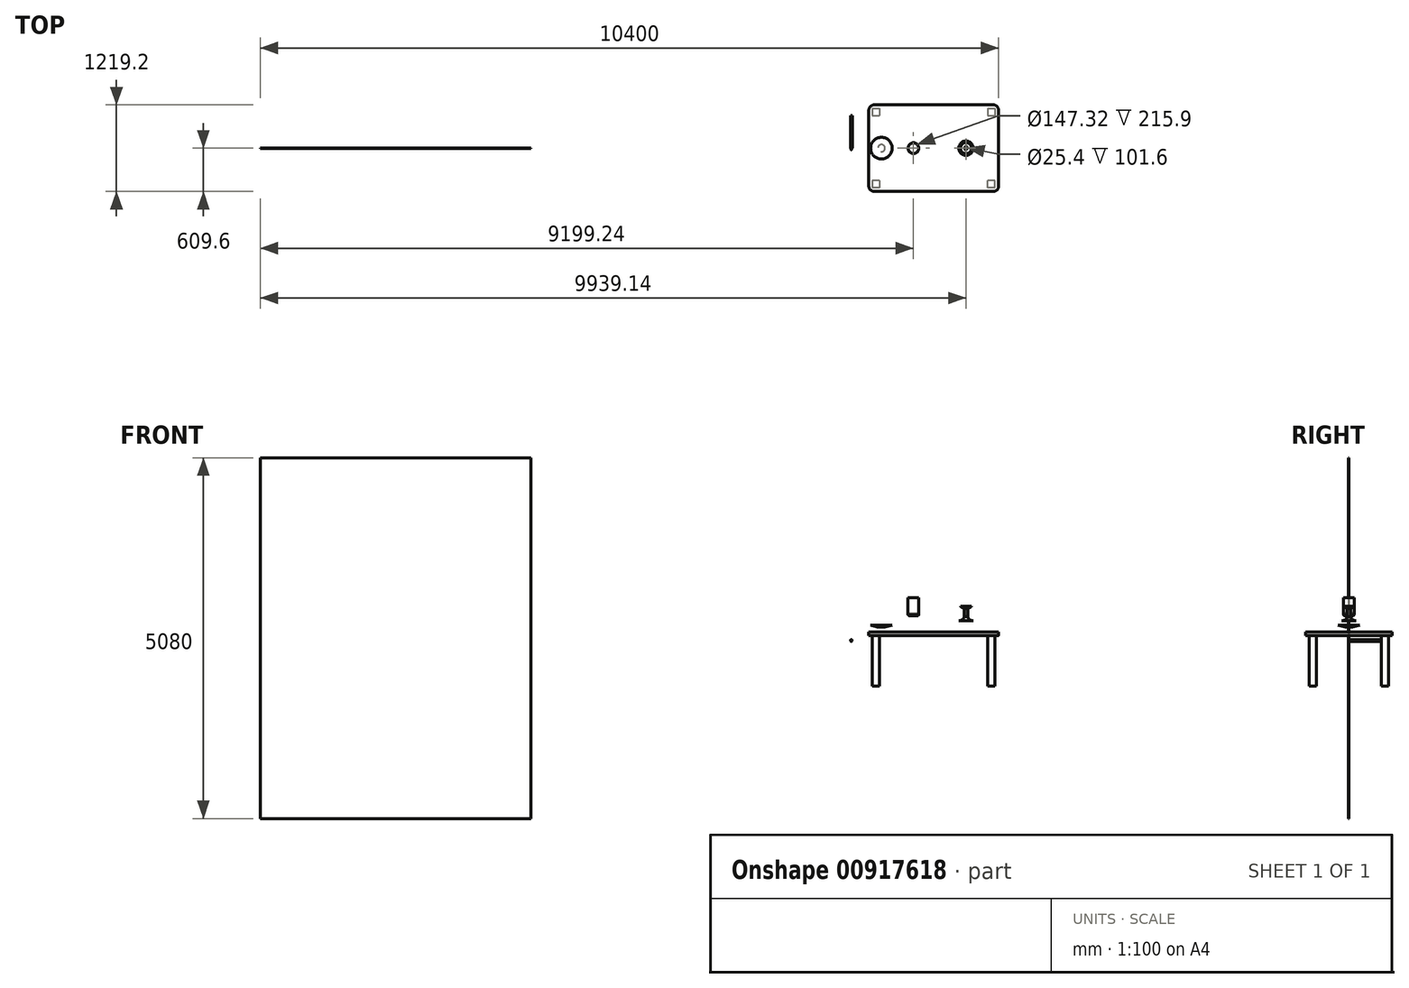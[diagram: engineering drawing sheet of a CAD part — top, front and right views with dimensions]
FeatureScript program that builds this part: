
annotation { "Feature Type Name" : "Feature", "Feature Type Description" : "" }
export const myFeature = defineFeature(function(context is Context, id is Id, definition is map)
    precondition{}
    {
        {
            var Q0;
            Q0=qCreatedBy(makeId("Top.planeOp"),FACE);
            var sketch = newSketch(context, id + "F0", { "sketchPlane" : qUnion([Q0])});
            skLineSegment(sketch, "E0.bottom", {"start": v(-838.2, 609.6) * mm, "end": v(838.2, 609.6) * mm});
            skLineSegment(sketch, "E0.top", {"start": v(-838.2, -609.6) * mm, "end": v(838.2, -609.6) * mm});
            skLineSegment(sketch, "E0.left", {"start": v(-914.4, 533.4) * mm, "end": v(-914.4, -533.4) * mm});
            skLineSegment(sketch, "E0.right", {"start": v(914.4, 533.4) * mm, "end": v(914.4, -533.4) * mm});
            skPoint(sketch, "E0.middle", {"position": v(0, 0) * mm});
            skLineSegment(sketch, "E1.bottom", {"start": v(-863.6, 558.8) * mm, "end": v(-762, 558.8) * mm});
            skLineSegment(sketch, "E1.top", {"start": v(-863.6, 457.2) * mm, "end": v(-762, 457.2) * mm});
            skLineSegment(sketch, "E1.left", {"start": v(-863.6, 558.8) * mm, "end": v(-863.6, 457.2) * mm});
            skLineSegment(sketch, "E1.right", {"start": v(-762, 558.8) * mm, "end": v(-762, 457.2) * mm});
            skLineSegment(sketch, "E2.bottom", {"start": v(762, 558.8) * mm, "end": v(863.6, 558.8) * mm});
            skLineSegment(sketch, "E2.top", {"start": v(762, 457.2) * mm, "end": v(863.6, 457.2) * mm});
            skLineSegment(sketch, "E2.left", {"start": v(762, 558.8) * mm, "end": v(762, 457.2) * mm});
            skLineSegment(sketch, "E2.right", {"start": v(863.6, 558.8) * mm, "end": v(863.6, 457.2) * mm});
            skLineSegment(sketch, "E3.bottom", {"start": v(863.6, -558.8) * mm, "end": v(762, -558.8) * mm});
            skLineSegment(sketch, "E3.top", {"start": v(863.6, -457.2) * mm, "end": v(762, -457.2) * mm});
            skLineSegment(sketch, "E3.left", {"start": v(863.6, -558.8) * mm, "end": v(863.6, -457.2) * mm});
            skLineSegment(sketch, "E3.right", {"start": v(762, -558.8) * mm, "end": v(762, -457.2) * mm});
            skLineSegment(sketch, "E4.bottom", {"start": v(-762, -457.2) * mm, "end": v(-863.6, -457.2) * mm});
            skLineSegment(sketch, "E4.top", {"start": v(-762, -558.8) * mm, "end": v(-863.6, -558.8) * mm});
            skLineSegment(sketch, "E4.left", {"start": v(-762, -457.2) * mm, "end": v(-762, -558.8) * mm});
            skLineSegment(sketch, "E4.right", {"start": v(-863.6, -457.2) * mm, "end": v(-863.6, -558.8) * mm});
            skPoint(sketch, "E5.visualSharp", {"position": v(-914.4, 609.6) * mm});
            skArc(sketch, "E5.filletArc", {"start": v(-838.2, 609.6) * mm, "mid": v(-892.08, 587.28) * mm, "end": v(-914.4, 533.4) * mm});
            skPoint(sketch, "E6.visualSharp", {"position": v(914.4, 609.6) * mm});
            skArc(sketch, "E6.filletArc", {"start": v(914.4, 533.4) * mm, "mid": v(892.08, 587.28) * mm, "end": v(838.2, 609.6) * mm});
            skPoint(sketch, "E7.visualSharp", {"position": v(914.4, -609.6) * mm});
            skArc(sketch, "E7.filletArc", {"start": v(838.2, -609.6) * mm, "mid": v(892.08, -587.28) * mm, "end": v(914.4, -533.4) * mm});
            skPoint(sketch, "E8.visualSharp", {"position": v(-914.4, -609.6) * mm});
            skArc(sketch, "E8.filletArc", {"start": v(-914.4, -533.4) * mm, "mid": v(-892.08, -587.28) * mm, "end": v(-838.2, -609.6) * mm});
            skSolve(sketch);
        }
        {
            var Q0;
            Q0=makeQuery(id+"F0.imprint","IMPRINT",FACE,{"disambiguationData":[TD([[makeQuery(id+"F0.imprint","IMPRINT",EDGE,{"derivedFrom":sQuery(id+"F0.wireOp",EDGE,"E0.bottom")}),-1.0]])]});
            var Q1;
            Q1=makeQuery(id+"F0.imprint","IMPRINT",FACE,{"disambiguationData":[TD([[makeQuery(id+"F0.imprint","IMPRINT",EDGE,{"derivedFrom":sQuery(id+"F0.wireOp",EDGE,"E4.bottom")}),1.0]])]});
            var Q2;
            Q2=makeQuery(id+"F0.imprint","IMPRINT",FACE,{"disambiguationData":[TD([[makeQuery(id+"F0.imprint","IMPRINT",EDGE,{"derivedFrom":sQuery(id+"F0.wireOp",EDGE,"E3.bottom")}),-1.0]])]});
            var Q3;
            Q3=makeQuery(id+"F0.imprint","IMPRINT",FACE,{"disambiguationData":[TD([[makeQuery(id+"F0.imprint","IMPRINT",EDGE,{"derivedFrom":sQuery(id+"F0.wireOp",EDGE,"E2.bottom")}),-1.0]])]});
            var Q4;
            Q4=makeQuery(id+"F0.imprint","IMPRINT",FACE,{"disambiguationData":[TD([[makeQuery(id+"F0.imprint","IMPRINT",EDGE,{"derivedFrom":sQuery(id+"F0.wireOp",EDGE,"E1.bottom")}),-1.0]])]});
            extrude(context, id + "F1", {"entities" : qUnion([Q0, Q1, Q2, Q3, Q4]), "depth" : 50.8 * mm, "offsetDistance" : 25.4 * mm});
        }
        {
            var Q0;
            Q0=makeQuery(id+"F0.imprint","IMPRINT",FACE,{"disambiguationData":[TD([[makeQuery(id+"F0.imprint","IMPRINT",EDGE,{"derivedFrom":sQuery(id+"F0.wireOp",EDGE,"E4.bottom")}),1.0]])]});
            var Q1;
            Q1=makeQuery(id+"F0.imprint","IMPRINT",FACE,{"disambiguationData":[TD([[makeQuery(id+"F0.imprint","IMPRINT",EDGE,{"derivedFrom":sQuery(id+"F0.wireOp",EDGE,"E1.bottom")}),-1.0]])]});
            var Q2;
            Q2=makeQuery(id+"F0.imprint","IMPRINT",FACE,{"disambiguationData":[TD([[makeQuery(id+"F0.imprint","IMPRINT",EDGE,{"derivedFrom":sQuery(id+"F0.wireOp",EDGE,"E2.bottom")}),-1.0]])]});
            var Q3;
            Q3=makeQuery(id+"F0.imprint","IMPRINT",FACE,{"disambiguationData":[TD([[makeQuery(id+"F0.imprint","IMPRINT",EDGE,{"derivedFrom":sQuery(id+"F0.wireOp",EDGE,"E3.bottom")}),-1.0]])]});
            extrude(context, id + "F2", {"entities" : qUnion([Q0, Q1, Q2, Q3]), "operationType" : NewBodyOperationType.ADD, "oppositeDirection" : true, "depth" : 711.2 * mm, "offsetDistance" : 25.4 * mm});
        }
        {
            var Q0;
            Q0=qCreatedBy(makeId("Front.planeOp"),FACE);
            var sketch = newSketch(context, id + "F3", { "sketchPlane" : qUnion([Q0])});
            skLineSegment(sketch, "E9", {"start": v(-286.32, 278.16) * mm, "end": v(-286.32, 532.16) * mm, "construction": true});
            skLineSegment(sketch, "E10.bottom", {"start": v(-286.32, 278.16) * mm, "end": v(-210.12, 278.16) * mm});
            skLineSegment(sketch, "E10.top", {"start": v(-286.32, 316.26) * mm, "end": v(-210.12, 316.26) * mm});
            skLineSegment(sketch, "E10.left", {"start": v(-286.32, 278.16) * mm, "end": v(-286.32, 316.26) * mm});
            skLineSegment(sketch, "E10.right", {"start": v(-210.12, 278.16) * mm, "end": v(-210.12, 316.26) * mm});
            skLineSegment(sketch, "E11.bottom", {"start": v(-210.12, 316.26) * mm, "end": v(-212.66, 316.26) * mm});
            skLineSegment(sketch, "E11.top", {"start": v(-210.12, 532.16) * mm, "end": v(-212.66, 532.16) * mm});
            skLineSegment(sketch, "E11.left", {"start": v(-210.12, 316.26) * mm, "end": v(-210.12, 532.16) * mm});
            skLineSegment(sketch, "E11.right", {"start": v(-212.66, 316.26) * mm, "end": v(-212.66, 532.16) * mm});
            skSolve(sketch);
        }
        {
            var Q0;
            Q0=makeQuery(id+"F3.imprint","IMPRINT",FACE,{"disambiguationData":[TD([[makeQuery(id+"F3.imprint","IMPRINT",EDGE,{"derivedFrom":sQuery(id+"F3.wireOp",EDGE,"E10.bottom")}),1.0]])]});
            var Q1;
            Q1=makeQuery(id+"F3.imprint","IMPRINT",FACE,{"disambiguationData":[TD([[makeQuery(id+"F3.imprint","IMPRINT",EDGE,{"derivedFrom":sQuery(id+"F3.wireOp",EDGE,"E11.top")}),1.0]])]});
            var Q2;
            Q2=sQuery(id+"F3.wireOp",EDGE,"E9");
            revolve(context, id + "F4", {"surfaceOperationType" : NewSurfaceOperationType.NEW, "entities" : qUnion([Q0, Q1]), "axis" : qUnion([Q2]), "revolveType" : RevolveType.FULL});
        }
        {
            var Q0;
            Q0=makeQuery(id+"F4.opRevolve","SWEPT_EDGE",EDGE,{"disambiguationData":[OSD([sQuery(id+"F3.wireOp",EDGE,"E10.bottom"),sQuery(id+"F3.wireOp",EDGE,"E10.right")])]});
            chamfer(context, id + "F5", {"entities" : qUnion([Q0]), "width" : 10.16 * mm, "tangentPropagation" : true});
        }
        {
            var Q0;
            Q0=qCreatedBy(makeId("Front.planeOp"),FACE);
            var sketch = newSketch(context, id + "F6", { "sketchPlane" : qUnion([Q0])});
            skLineSegment(sketch, "E12", {"start": v(-736.83, 117.03) * mm, "end": v(-736.83, 258.84) * mm});
            skLineSegment(sketch, "E13", {"start": v(-736.83, 117.03) * mm, "end": v(-787.63, 117.03) * mm});
            skLineSegment(sketch, "E14", {"start": v(-787.63, 117.03) * mm, "end": v(-889.23, 144.25) * mm});
            skLineSegment(sketch, "E15", {"start": v(-889.23, 144.25) * mm, "end": v(-736.83, 119.57) * mm});
            skSolve(sketch);
        }
        {
            var Q0;
            {var subQ0=sQuery(id+"F6.wireOp",EDGE,"E13");Q0=makeQuery(id+"F6.imprint","IMPRINT",FACE,{"disambiguationData":[TD([[makeQuery(id+"F6.imprint","IMPRINT",EDGE,{"derivedFrom":subQ0}),-1.0]])]});}
            var Q1;
            Q1=sQuery(id+"F6.wireOp",EDGE,"E12");
            revolve(context, id + "F7", {"surfaceOperationType" : NewSurfaceOperationType.NEW, "entities" : qUnion([Q0]), "axis" : qUnion([Q1]), "revolveType" : RevolveType.FULL});
        }
        {
            var Q0;
            Q0=qCreatedBy(makeId("Front.planeOp"),FACE);
            var sketch = newSketch(context, id + "F8", { "sketchPlane" : qUnion([Q0])});
            skCircle(sketch, "E16", {"center": v(-1161.66, -71.9) * mm, "radius": 12.7 * mm});
            skCircle(sketch, "E17", {"center": v(-1161.66, -71.9) * mm, "radius": 1.27 * mm});
            skSolve(sketch);
        }
        {
            var Q0;
            Q0=makeQuery(id+"F8.imprint","IMPRINT",FACE,{"disambiguationData":[TD([[makeQuery(id+"F8.imprint","IMPRINT",EDGE,{"derivedFrom":sQuery(id+"F8.wireOp",EDGE,"E16")}),1.0]])]});
            var Q1;
            Q1=makeQuery(id+"F8.imprint","IMPRINT",FACE,{"disambiguationData":[TD([[makeQuery(id+"F8.imprint","IMPRINT",EDGE,{"derivedFrom":sQuery(id+"F8.wireOp",EDGE,"E17")}),1.0]])]});
            extrude(context, id + "F9", {"entities" : qUnion([Q0, Q1]), "oppositeDirection" : true, "depth" : 457.2 * mm, "offsetDistance" : 25.4 * mm});
        }
        {
            var Q0;
            Q0=makeQuery(id+"F8.imprint","IMPRINT",FACE,{"disambiguationData":[TD([[makeQuery(id+"F8.imprint","IMPRINT",EDGE,{"derivedFrom":sQuery(id+"F8.wireOp",EDGE,"E17")}),1.0]])]});
            extrude(context, id + "F10", {"entities" : qUnion([Q0]), "operationType" : NewBodyOperationType.ADD, "depth" : 25.4 * mm, "offsetDistance" : 25.4 * mm});
        }
        {
            var Q0;
            Q0=makeQuery(id+"F9.opExtrude","CAP_EDGE",EDGE,{"disambiguationData":[OSD([sQuery(id+"F8.wireOp",EDGE,"E16")])],"isStart":true});
            fillet(context, id + "F11", {"entities" : qUnion([Q0]), "radius" : 2.54 * mm, "tangentPropagation" : true, "allowEdgeOverflow" : false});
        }
        {
            var Q0;
            Q0=qCreatedBy(makeId("Front.planeOp"),FACE);
            var sketch = newSketch(context, id + "F12", { "sketchPlane" : qUnion([Q0])});
            skLineSegment(sketch, "E18", {"start": v(453.58, 205.76) * mm, "end": v(453.58, 408.96) * mm});
            skLineSegment(sketch, "E19", {"start": v(453.58, 205.76) * mm, "end": v(351.98, 205.76) * mm});
            skLineSegment(sketch, "E20.bottom", {"start": v(453.58, 260.73) * mm, "end": v(428.18, 260.73) * mm});
            skLineSegment(sketch, "E20.top", {"start": v(453.58, 376.7) * mm, "end": v(428.18, 376.7) * mm});
            skLineSegment(sketch, "E20.left", {"start": v(453.58, 260.73) * mm, "end": v(453.58, 376.7) * mm});
            skLineSegment(sketch, "E20.right", {"start": v(428.18, 260.73) * mm, "end": v(428.18, 376.7) * mm});
            skLineSegment(sketch, "E21.bottom", {"start": v(453.58, 376.7) * mm, "end": v(420.56, 376.7) * mm});
            skLineSegment(sketch, "E21.top", {"start": v(453.58, 389.4) * mm, "end": v(420.56, 389.4) * mm});
            skLineSegment(sketch, "E21.left", {"start": v(453.58, 376.7) * mm, "end": v(453.58, 389.4) * mm});
            skLineSegment(sketch, "E21.right", {"start": v(420.56, 376.7) * mm, "end": v(420.56, 389.4) * mm});
            skLineSegment(sketch, "E22", {"start": v(504.49, 408.96) * mm, "end": v(355.03, 408.96) * mm});
            skArc(sketch, "E23", {"start": v(375.65, 408.96) * mm, "mid": v(396.06, 394.5) * mm, "end": v(420.56, 389.4) * mm});
            skArc(sketch, "E24", {"start": v(351.98, 205.76) * mm, "mid": v(398.96, 220.93) * mm, "end": v(428.18, 260.73) * mm});
            skLineSegment(sketch, "E25", {"start": v(375.65, 408.96) * mm, "end": v(437.07, 389.4) * mm});
            skSolve(sketch);
        }
        {
            var Q0;
            {var subQ3=sQuery(id+"F12.wireOp",EDGE,"E20.top");Q0=makeQuery(id+"F12.imprint","IMPRINT",FACE,{"disambiguationData":[TD([[makeQuery(id+"F12.imprint","IMPRINT",EDGE,{"derivedFrom":subQ3}),-1.0]])]});}
            var Q1;
            {var subQ0=sQuery(id+"F12.wireOp",EDGE,"E20.bottom");Q1=makeQuery(id+"F12.imprint","IMPRINT",FACE,{"disambiguationData":[TD([[makeQuery(id+"F12.imprint","IMPRINT",EDGE,{"derivedFrom":subQ0}),-1.0]])]});}
            var Q2;
            {var subQ2=sQuery(id+"F12.wireOp",EDGE,"E19");Q2=makeQuery(id+"F12.imprint","IMPRINT",FACE,{"disambiguationData":[TD([[makeQuery(id+"F12.imprint","IMPRINT",EDGE,{"derivedFrom":subQ2}),-1.0]])]});}
            var Q3;
            {var subQ2=sQuery(id+"F12.wireOp",EDGE,"E23");Q3=makeQuery(id+"F12.imprint","IMPRINT",FACE,{"disambiguationData":[TD([[makeQuery(id+"F12.imprint","IMPRINT",EDGE,{"derivedFrom":subQ2}),1.0]])]});}
            var Q4;
            Q4=sQuery(id+"F12.wireOp",EDGE,"E18");
            revolve(context, id + "F13", {"surfaceOperationType" : NewSurfaceOperationType.NEW, "entities" : qUnion([Q0, Q1, Q2, Q3]), "axis" : qUnion([Q4]), "revolveType" : RevolveType.FULL});
        }
        {
            var Q0;
            Q0=makeQuery(id+"F13.opRevolve","SWEPT_FACE",FACE,{"disambiguationData":[OSD([sQuery(id+"F12.wireOp",EDGE,"E21.top")])]});
            var sketch = newSketch(context, id + "F14", { "sketchPlane" : qUnion([Q0])});
            skCircle(sketch, "E26", {"center": v(453.58, 0) * mm, "radius": 12.7 * mm});
            skSolve(sketch);
        }
        {
            var Q0;
            Q0=makeQuery(id+"F14.imprint","IMPRINT",FACE,{"disambiguationData":[TD([[makeQuery(id+"F14.imprint","IMPRINT",EDGE,{"derivedFrom":sQuery(id+"F14.wireOp",EDGE,"E26")}),1.0]])]});
            extrude(context, id + "F15", {"entities" : qUnion([Q0]), "operationType" : NewBodyOperationType.REMOVE, "oppositeDirection" : true, "depth" : 101.6 * mm, "offsetDistance" : 25.4 * mm});
        }
        {
            var Q0;
            Q0=qCreatedBy(makeId("Front.planeOp"),FACE);
            var sketch = newSketch(context, id + "F16", { "sketchPlane" : qUnion([Q0])});
            skLineSegment(sketch, "E27.bottom", {"start": v(-5675.56, 2500.27) * mm, "end": v(-9485.56, 2500.27) * mm});
            skLineSegment(sketch, "E27.top", {"start": v(-5675.56, -2579.73) * mm, "end": v(-9485.56, -2579.73) * mm});
            skLineSegment(sketch, "E27.left", {"start": v(-5675.56, 2500.27) * mm, "end": v(-5675.56, -2579.73) * mm});
            skLineSegment(sketch, "E27.right", {"start": v(-9485.56, 2500.27) * mm, "end": v(-9485.56, -2579.73) * mm});
            skSolve(sketch);
        }
        {
            var Q0;
            Q0 = qSketchRegion(id + "F16", true);
            extrude(context, id + "F17", {"entities" : qUnion([Q0]), "depth" : 6.35 * mm, "offsetDistance" : 25.4 * mm});
        }
    });
